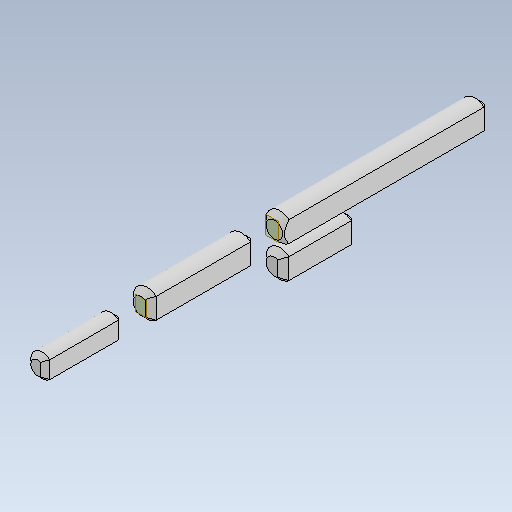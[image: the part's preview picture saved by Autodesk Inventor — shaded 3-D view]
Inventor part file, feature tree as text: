
AUTODESK INVENTOR PART (.ipt)
format: ipt  version: 2023 (Build 270158030, 158C)  size: 207,360 bytes
history: native  units: mm
features: projected_geometry x10, other x4, extrude x4, sketch x4, chamfer x3, plane x2
ambient origin geometry x8: Origin, YZ Plane, XZ Plane, XY Plane, X Axis, Y Axis, Z Axis, Center Point
bodies: Body1 (feature_tree), Body2 (feature_tree), Body3 (feature_tree), Body4 (feature_tree)
feature tree (27):
  other  "5x17mm"
  extrude  "Extrusion1"  Depth=26.0mm
  chamfer  "Chamfer1"  Distance=5.0mm
  plane  "Work Plane1"
  extrude  "Extrusion2"  Depth=5.0mm
  chamfer  "Chamfer2"  Distance=6.0mm
  plane  "Work Plane2"
  extrude  "Extrusion3"  Depth=6.0mm
  extrude  "Extrusion4"  Depth=2.0mm TaperAngle=0.0deg
  chamfer  "Chamfer3"  Distance=2.0mm Angle=45.0deg
  sketch  "Sketch1"  dims[d0=5.0mm d1=26.0mm]
  sketch  "Sketch2"  dims[d2=1.65mm d3=5.0mm d4=1.65mm]
  sketch  "Sketch3"  dims[d5=5.0mm d6=1.65mm d7=5.0mm d8=1.65mm]
  projected_geometry  "Projected Loop1"
  projected_geometry  "Projected Loop2"
  projected_geometry  "Projected Loop3"
  projected_geometry  "Projected Loop4"
  sketch  "Sketch4"  dims[d9=6.0mm d10=6.0mm d11=6.0mm d12=17.0mm d13=0.0mm d14=1.0mm d15=2.0mm d16=45.0deg d17=6.0mm d18=6.0mm d19=1.98mm d20=6.0mm d21=1.98mm d22=7.0mm d23=6.0mm d24=1.98mm d25=6.0mm d26=1.98mm d27=7.0mm d28=7.0mm d29=23.0mm d30=0.0mm d31=1.2mm d32=2.0mm d33=45.0deg d34=6.0mm d35=45.0mm d36=0.0mm d37=16.0mm d38=0.0mm d39=1.2mm d40=2.0mm d41=45.0deg]
  projected_geometry  "Projected Loop5"
  projected_geometry  "Projected Loop6"
  projected_geometry  "Projected Loop7"
  projected_geometry  "Projected Loop8"
  projected_geometry  "Projected Loop9"
  projected_geometry  "Projected Loop10"
  other  "6x23mm"
  other  "6x16mm"
  other  "6x45mm"
